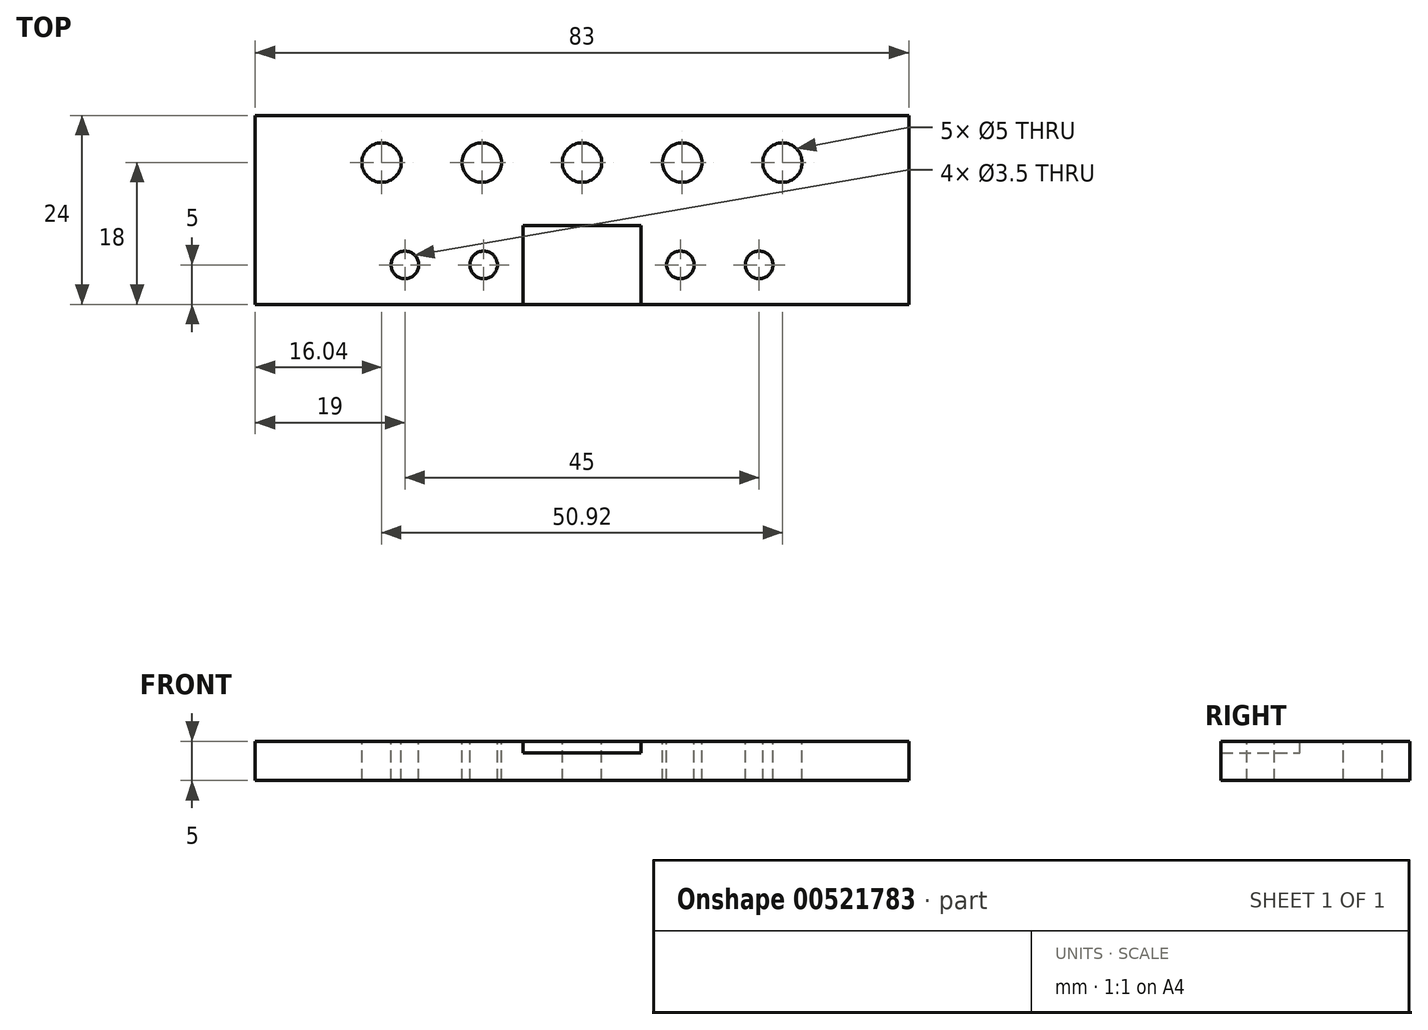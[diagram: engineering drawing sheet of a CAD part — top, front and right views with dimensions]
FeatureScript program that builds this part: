
annotation { "Feature Type Name" : "Feature", "Feature Type Description" : "" }
export const myFeature = defineFeature(function(context is Context, id is Id, definition is map)
    precondition{}
    {
        {
            var Q0;
            Q0=qCreatedBy(makeId("Top.planeOp"),FACE);
            var sketch = newSketch(context, id + "F0", { "sketchPlane" : qUnion([Q0])});
            skLineSegment(sketch, "E0.bottom", {"start": v(32.5, 5) * mm, "end": v(-32.5, 5) * mm});
            skLineSegment(sketch, "E0.top", {"start": v(32.5, -5) * mm, "end": v(-32.5, -5) * mm});
            skLineSegment(sketch, "E0.left", {"start": v(32.5, 5) * mm, "end": v(32.5, -5) * mm});
            skLineSegment(sketch, "E0.right", {"start": v(-32.5, 5) * mm, "end": v(-32.5, -5) * mm});
            skPoint(sketch, "E0.middle", {"position": v(0, 0) * mm});
            skSolve(sketch);
        }
        {
            var Q0;
            Q0 = qSketchRegion(id + "F0", true);
            extrude(context, id + "F1", {"entities" : qUnion([Q0]), "depth" : 10 * mm, "offsetDistance" : 25 * mm});
        }
        {
            var Q0;
            Q0=makeQuery(id+"F1.opExtrude","CAP_FACE",FACE,{"disambiguationData":[OSD([sQuery(id+"F0.wireOp",EDGE,"E0.bottom"),sQuery(id+"F0.wireOp",EDGE,"E0.top"),sQuery(id+"F0.wireOp",EDGE,"E0.left"),sQuery(id+"F0.wireOp",EDGE,"E0.right")])],"isStart":false});
            var sketch = newSketch(context, id + "F2", { "sketchPlane" : qUnion([Q0])});
            skPoint(sketch, "E1", {"position": v(-12.5, 0) * mm});
            skPoint(sketch, "E1.positionSnap0", {"position": v(-32.5, 0) * mm});
            skPoint(sketch, "E2", {"position": v(-22.5, 0) * mm});
            skPoint(sketch, "E3", {"position": v(22.5, 0) * mm});
            skPoint(sketch, "E3.positionSnap0", {"position": v(32.5, 0) * mm});
            skPoint(sketch, "E4", {"position": v(12.5, 0) * mm});
            skPoint(sketch, "E5", {"position": v(7.5, 0) * mm});
            skPoint(sketch, "E6", {"position": v(-7.5, 0) * mm});
            skLineSegment(sketch, "E7", {"start": v(-7.5, -5) * mm, "end": v(-7.5, 5) * mm});
            skLineSegment(sketch, "E8", {"start": v(7.5, -5) * mm, "end": v(7.5, 5) * mm});
            skCircle(sketch, "E9", {"center": v(-22.5, 0) * mm, "radius": 1.75 * mm});
            skCircle(sketch, "E10", {"center": v(-12.5, 0) * mm, "radius": 1.75 * mm});
            skCircle(sketch, "E11", {"center": v(12.5, 0) * mm, "radius": 1.75 * mm});
            skCircle(sketch, "E12", {"center": v(22.5, 0) * mm, "radius": 1.75 * mm});
            skSolve(sketch);
        }
        {
            var Q0;
            {var subQ0=sQuery(id+"F2.wireOp",EDGE,"E7");Q0=makeQuery(id+"F2.imprint","IMPRINT",FACE,{"disambiguationData":[TD([[makeQuery(id+"F2.imprint","IMPRINT",EDGE,{"derivedFrom":subQ0}),-1.0]])]});}
            extrude(context, id + "F3", {"entities" : qUnion([Q0]), "operationType" : NewBodyOperationType.REMOVE, "oppositeDirection" : true, "depth" : 3 * mm, "offsetDistance" : 25 * mm});
        }
        {
            var Q0;
            Q0=makeQuery(id+"F2.imprint","IMPRINT",FACE,{"disambiguationData":[TD([[makeQuery(id+"F2.imprint","IMPRINT",EDGE,{"derivedFrom":sQuery(id+"F2.wireOp",EDGE,"E9")}),1.0]])]});
            var Q1;
            Q1=makeQuery(id+"F2.imprint","IMPRINT",FACE,{"disambiguationData":[TD([[makeQuery(id+"F2.imprint","IMPRINT",EDGE,{"derivedFrom":sQuery(id+"F2.wireOp",EDGE,"E10")}),1.0]])]});
            var Q2;
            Q2=makeQuery(id+"F2.imprint","IMPRINT",FACE,{"disambiguationData":[TD([[makeQuery(id+"F2.imprint","IMPRINT",EDGE,{"derivedFrom":sQuery(id+"F2.wireOp",EDGE,"E11")}),1.0]])]});
            var Q3;
            Q3=makeQuery(id+"F2.imprint","IMPRINT",FACE,{"disambiguationData":[TD([[makeQuery(id+"F2.imprint","IMPRINT",EDGE,{"derivedFrom":sQuery(id+"F2.wireOp",EDGE,"E12")}),1.0]])]});
            extrude(context, id + "F4", {"entities" : qUnion([Q0, Q1, Q2, Q3]), "operationType" : NewBodyOperationType.REMOVE, "oppositeDirection" : true, "depth" : 25 * mm, "offsetDistance" : 25 * mm});
        }
        {
            var Q0;
            Q0=makeQuery(id+"F1.opExtrude","SWEPT_FACE",FACE,{"disambiguationData":[OSD([sQuery(id+"F0.wireOp",EDGE,"E0.left")])]});
            extrude(context, id + "F5", {"entities" : qUnion([Q0]), "operationType" : NewBodyOperationType.ADD, "depth" : 9 * mm, "offsetDistance" : 25 * mm});
        }
        {
            var Q0;
            Q0=makeQuery(id+"F1.opExtrude","SWEPT_FACE",FACE,{"disambiguationData":[OSD([sQuery(id+"F0.wireOp",EDGE,"E0.right")])]});
            extrude(context, id + "F6", {"entities" : qUnion([Q0]), "operationType" : NewBodyOperationType.ADD, "depth" : 9 * mm, "offsetDistance" : 25 * mm});
        }
        {
            var Q0;
            {var subQ0=sQuery(id+"F0.wireOp",EDGE,"E0.right");var subQ1=sQuery(id+"F0.wireOp",EDGE,"E0.left");Q0=makeQuery(id+"F6.boolean.opBoolean","MERGE",FACE,{"derivedFrom":[makeQuery(id+"F5.boolean.opBoolean","MERGE",FACE,{"derivedFrom":[makeQuery(id+"F1.opExtrude","CAP_FACE",FACE,{"disambiguationData":[OSD([sQuery(id+"F0.wireOp",EDGE,"E0.bottom"),sQuery(id+"F0.wireOp",EDGE,"E0.top"),subQ1,subQ0])],"isStart":true}),makeQuery(id+"F5.opExtrude","SWEPT_FACE",FACE,{"disambiguationData":[OSD([subQ1]),TDD([makeQuery(id+"F1.opExtrude","CAP_EDGE",EDGE,{"disambiguationData":[OSD([subQ1])],"isStart":true})])]})]}),makeQuery(id+"F6.opExtrude","SWEPT_FACE",FACE,{"disambiguationData":[OSD([subQ0]),TDD([makeQuery(id+"F1.opExtrude","CAP_EDGE",EDGE,{"disambiguationData":[OSD([subQ0])],"isStart":true})])]})]});}
            extrude(context, id + "F7", {"entities" : qUnion([Q0]), "operationType" : NewBodyOperationType.REMOVE, "oppositeDirection" : true, "depth" : 5 * mm, "offsetDistance" : 25 * mm});
        }
        {
            var Q0;
            Q0=makeQuery(id+"F3.boolean.opBoolean","COPY",FACE,{"derivedFrom":makeQuery(id+"F3.opExtrude","CAP_FACE",FACE,{"disambiguationData":[OSD([sQuery(id+"F0.wireOp",EDGE,"E0.bottom"),sQuery(id+"F0.wireOp",EDGE,"E0.top"),sQuery(id+"F2.wireOp",EDGE,"E7"),sQuery(id+"F2.wireOp",EDGE,"E8")])],"isStart":false})});
            extrude(context, id + "F8", {"entities" : qUnion([Q0]), "operationType" : NewBodyOperationType.ADD, "depth" : 1.5 * mm, "offsetDistance" : 25 * mm});
        }
        {
            var Q0;
            {var subQ0=sQuery(id+"F0.wireOp",EDGE,"E0.bottom");Q0=makeQuery(id+"F8.boolean.opBoolean","MERGE",FACE,{"derivedFrom":[makeQuery(id+"F6.boolean.opBoolean","MERGE",FACE,{"derivedFrom":[makeQuery(id+"F5.boolean.opBoolean","MERGE",FACE,{"derivedFrom":[makeQuery(id+"F1.opExtrude","SWEPT_FACE",FACE,{"disambiguationData":[OSD([subQ0])]}),makeQuery(id+"F5.opExtrude","SWEPT_FACE",FACE,{"disambiguationData":[OSD([subQ0,sQuery(id+"F0.wireOp",EDGE,"E0.left")])]})]}),makeQuery(id+"F6.opExtrude","SWEPT_FACE",FACE,{"disambiguationData":[OSD([subQ0,sQuery(id+"F0.wireOp",EDGE,"E0.right")])]})]}),makeQuery(id+"F8.opExtrude","SWEPT_FACE",FACE,{"disambiguationData":[OSD([subQ0])]})]});}
            var sketch = newSketch(context, id + "F9", { "sketchPlane" : qUnion([Q0])});
            skLineSegment(sketch, "E13.bottom", {"start": v(-41.5, 10) * mm, "end": v(41.5, 10) * mm});
            skLineSegment(sketch, "E13.top", {"start": v(-41.5, 5) * mm, "end": v(41.5, 5) * mm});
            skLineSegment(sketch, "E13.left", {"start": v(-41.5, 10) * mm, "end": v(-41.5, 5) * mm});
            skLineSegment(sketch, "E13.right", {"start": v(41.5, 10) * mm, "end": v(41.5, 5) * mm});
            skSolve(sketch);
        }
        {
            var Q0;
            Q0 = qSketchRegion(id + "F9", true);
            extrude(context, id + "F10", {"entities" : qUnion([Q0]), "operationType" : NewBodyOperationType.ADD, "depth" : 14 * mm, "offsetDistance" : 25 * mm});
        }
        {
            var Q0;
            {var subQ0=sQuery(id+"F0.wireOp",EDGE,"E0.right");var subQ1=sQuery(id+"F0.wireOp",EDGE,"E0.bottom");var subQ3=sQuery(id+"F0.wireOp",EDGE,"E0.top");var subQ5=sQuery(id+"F0.wireOp",EDGE,"E0.left");var subQ6=makeQuery(id+"F1.opExtrude","CAP_FACE",FACE,{"disambiguationData":[OSD([subQ1,subQ3,subQ5,subQ0])],"isStart":false});Q0=makeQuery(id+"F10.boolean.opBoolean","MERGE",FACE,{"derivedFrom":[makeQuery(id+"F5.boolean.opBoolean","MERGE",FACE,{"derivedFrom":[makeQuery(id+"F3.boolean.opBoolean","SPLIT",FACE,{"disambiguationData":[TD([makeQuery(id+"F1.opExtrude","SWEPT_FACE",FACE,{"disambiguationData":[OSD([subQ5])]})])],"derivedFrom":subQ6}),makeQuery(id+"F5.opExtrude","SWEPT_FACE",FACE,{"disambiguationData":[OSD([subQ5]),TDD([makeQuery(id+"F1.opExtrude","CAP_EDGE",EDGE,{"disambiguationData":[OSD([subQ5])],"isStart":false})])]})]}),makeQuery(id+"F6.boolean.opBoolean","MERGE",FACE,{"derivedFrom":[makeQuery(id+"F3.boolean.opBoolean","SPLIT",FACE,{"disambiguationData":[TD([makeQuery(id+"F1.opExtrude","SWEPT_FACE",FACE,{"disambiguationData":[OSD([subQ0])]})])],"derivedFrom":subQ6}),makeQuery(id+"F6.opExtrude","SWEPT_FACE",FACE,{"disambiguationData":[OSD([subQ0]),TDD([makeQuery(id+"F1.opExtrude","CAP_EDGE",EDGE,{"disambiguationData":[OSD([subQ0])],"isStart":false})])]})]}),makeQuery(id+"F10.opExtrude","SWEPT_FACE",FACE,{"disambiguationData":[OSD([sQuery(id+"F9.wireOp",EDGE,"E13.bottom")])]})]});}
            var sketch = newSketch(context, id + "F11", { "sketchPlane" : qUnion([Q0])});
            skPoint(sketch, "E14", {"position": v(0, 19) * mm});
            skPoint(sketch, "E15", {"position": v(0, 13) * mm});
            skCircle(sketch, "E16", {"center": v(0, 13) * mm, "radius": 2.5 * mm});
            skPoint(sketch, "E17", {"position": v(-12.73, 13) * mm});
            skPoint(sketch, "E18", {"position": v(-25.46, 13) * mm});
            skPoint(sketch, "E19", {"position": v(12.73, 13) * mm});
            skPoint(sketch, "E20", {"position": v(25.46, 13) * mm});
            skCircle(sketch, "E21", {"center": v(-25.46, 13) * mm, "radius": 2.5 * mm});
            skCircle(sketch, "E22", {"center": v(-12.73, 13) * mm, "radius": 2.5 * mm});
            skCircle(sketch, "E23", {"center": v(12.73, 13) * mm, "radius": 2.5 * mm});
            skCircle(sketch, "E24", {"center": v(25.46, 13) * mm, "radius": 2.5 * mm});
            skSolve(sketch);
        }
        {
            var Q0;
            Q0=makeQuery(id+"F11.imprint","IMPRINT",FACE,{"disambiguationData":[TD([[makeQuery(id+"F11.imprint","IMPRINT",EDGE,{"derivedFrom":sQuery(id+"F11.wireOp",EDGE,"E23")}),1.0]])]});
            var Q1;
            Q1=makeQuery(id+"F11.imprint","IMPRINT",FACE,{"disambiguationData":[TD([[makeQuery(id+"F11.imprint","IMPRINT",EDGE,{"derivedFrom":sQuery(id+"F11.wireOp",EDGE,"E24")}),1.0]])]});
            var Q2;
            Q2=makeQuery(id+"F11.imprint","IMPRINT",FACE,{"disambiguationData":[TD([[makeQuery(id+"F11.imprint","IMPRINT",EDGE,{"derivedFrom":sQuery(id+"F11.wireOp",EDGE,"E16")}),1.0]])]});
            var Q3;
            Q3=makeQuery(id+"F11.imprint","IMPRINT",FACE,{"disambiguationData":[TD([[makeQuery(id+"F11.imprint","IMPRINT",EDGE,{"derivedFrom":sQuery(id+"F11.wireOp",EDGE,"E22")}),1.0]])]});
            var Q4;
            Q4=makeQuery(id+"F11.imprint","IMPRINT",FACE,{"disambiguationData":[TD([[makeQuery(id+"F11.imprint","IMPRINT",EDGE,{"derivedFrom":sQuery(id+"F11.wireOp",EDGE,"E21")}),1.0]])]});
            extrude(context, id + "F12", {"entities" : qUnion([Q0, Q1, Q2, Q3, Q4]), "operationType" : NewBodyOperationType.REMOVE, "oppositeDirection" : true, "depth" : 25 * mm, "offsetDistance" : 25 * mm});
        }
    });
